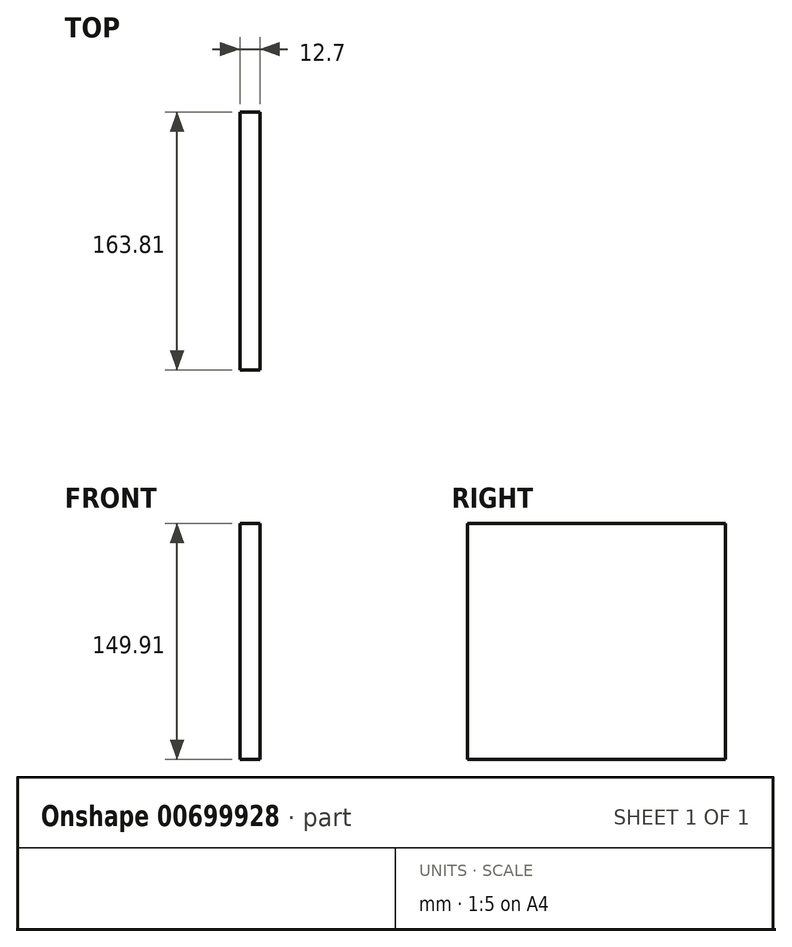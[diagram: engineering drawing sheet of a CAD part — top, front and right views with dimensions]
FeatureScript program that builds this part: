
annotation { "Feature Type Name" : "Feature", "Feature Type Description" : "" }
export const myFeature = defineFeature(function(context is Context, id is Id, definition is map)
    precondition{}
    {
        {
            var Q0;
            Q0=qCreatedBy(makeId("Right.planeOp"),FACE);
            var sketch = newSketch(context, id + "F0", { "sketchPlane" : qUnion([Q0])});
            skLineSegment(sketch, "E0.bottom", {"start": v(-68.63, 70.78) * mm, "end": v(95.18, 70.78) * mm});
            skLineSegment(sketch, "E0.top", {"start": v(-68.63, -79.13) * mm, "end": v(95.18, -79.13) * mm});
            skLineSegment(sketch, "E0.left", {"start": v(-68.63, 70.78) * mm, "end": v(-68.63, -79.13) * mm});
            skLineSegment(sketch, "E0.right", {"start": v(95.18, 70.78) * mm, "end": v(95.18, -79.13) * mm});
            skSolve(sketch);
        }
        {
            var Q0;
            Q0=makeQuery(id+"F0.imprint","IMPRINT",FACE,{"disambiguationData":[TD([[makeQuery(id+"F0.imprint","IMPRINT",EDGE,{"derivedFrom":sQuery(id+"F0.wireOp",EDGE,"E0.bottom")}),-1.0]])]});
            extrude(context, id + "F1", {"entities" : qUnion([Q0]), "depth" : 12.7 * mm, "offsetDistance" : 25.4 * mm});
        }
    });
